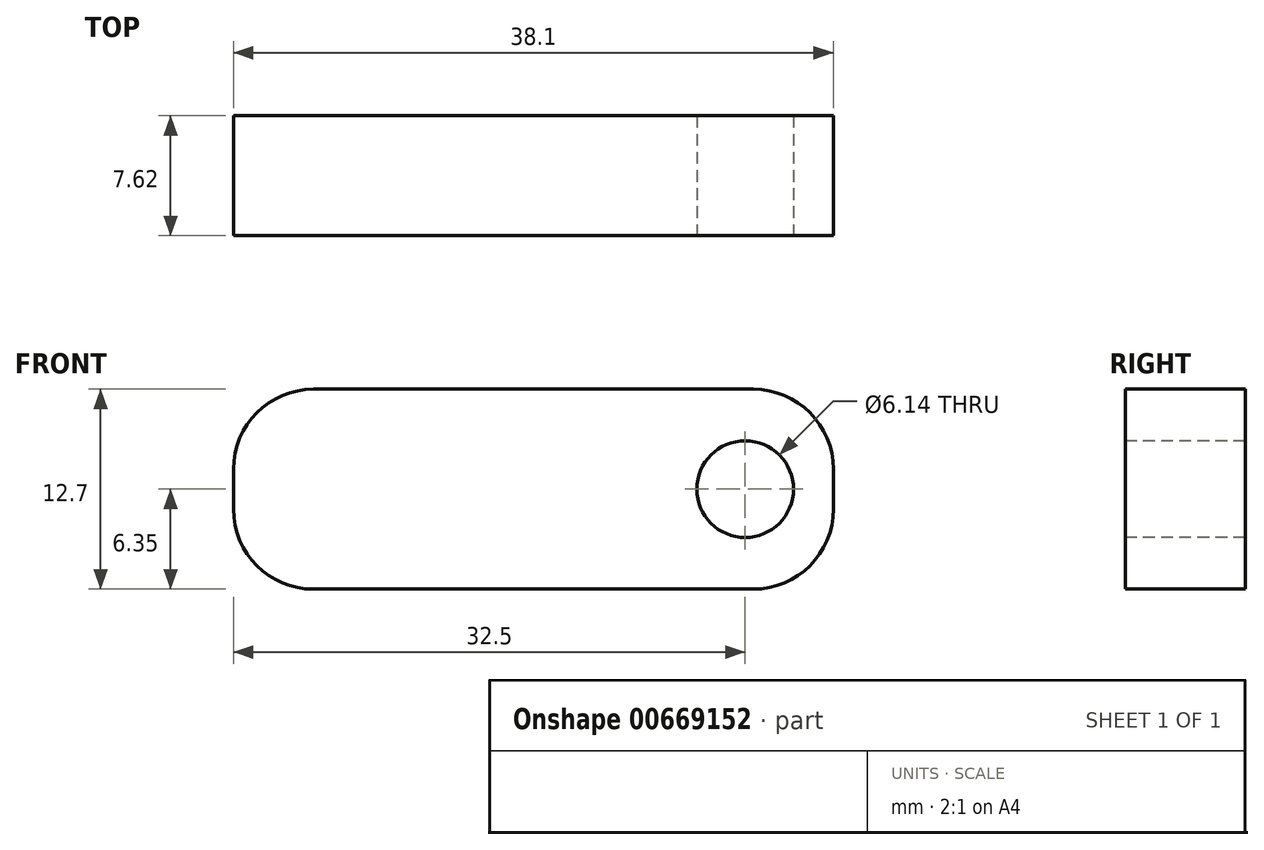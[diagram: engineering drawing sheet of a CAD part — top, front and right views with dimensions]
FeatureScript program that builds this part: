
annotation { "Feature Type Name" : "Feature", "Feature Type Description" : "" }
export const myFeature = defineFeature(function(context is Context, id is Id, definition is map)
    precondition{}
    {
        {
            var Q0;
            Q0=qCreatedBy(makeId("Front.planeOp"),FACE);
            var sketch = newSketch(context, id + "F0", { "sketchPlane" : qUnion([Q0])});
            skLineSegment(sketch, "E0.bottom", {"start": v(0, 0) * mm, "end": v(-38.1, 0) * mm});
            skLineSegment(sketch, "E0.top", {"start": v(0, 12.7) * mm, "end": v(-38.1, 12.7) * mm});
            skLineSegment(sketch, "E0.left", {"start": v(0, 0) * mm, "end": v(0, 12.7) * mm});
            skLineSegment(sketch, "E0.right", {"start": v(-38.1, 0) * mm, "end": v(-38.1, 12.7) * mm});
            skSolve(sketch);
        }
        {
            var Q0;
            Q0=makeQuery(id+"F0.imprint","IMPRINT",FACE,{"disambiguationData":[TD([[makeQuery(id+"F0.imprint","IMPRINT",EDGE,{"derivedFrom":sQuery(id+"F0.wireOp",EDGE,"E0.bottom")}),-1.0]])]});
            extrude(context, id + "F1", {"entities" : qUnion([Q0]), "depth" : 7.62 * mm, "offsetDistance" : 25.4 * mm});
        }
        {
            var Q0;
            Q0=makeQuery(id+"F1.opExtrude","CAP_FACE",FACE,{"disambiguationData":[OSD([sQuery(id+"F0.wireOp",EDGE,"E0.bottom"),sQuery(id+"F0.wireOp",EDGE,"E0.top"),sQuery(id+"F0.wireOp",EDGE,"E0.left"),sQuery(id+"F0.wireOp",EDGE,"E0.right")])],"isStart":false});
            var sketch = newSketch(context, id + "F2", { "sketchPlane" : qUnion([Q0])});
            skCircle(sketch, "E1", {"center": v(-5.6, 6.35) * mm, "radius": 3.07 * mm});
            skPoint(sketch, "E1.centerSnap0", {"position": v(0, 6.35) * mm});
            skSolve(sketch);
        }
        {
            var Q0;
            Q0=makeQuery(id+"F2.imprint","IMPRINT",FACE,{"disambiguationData":[TD([[makeQuery(id+"F2.imprint","IMPRINT",EDGE,{"derivedFrom":sQuery(id+"F2.wireOp",EDGE,"E1")}),1.0]])]});
            extrude(context, id + "F3", {"entities" : qUnion([Q0]), "operationType" : NewBodyOperationType.REMOVE, "endBound" : BoundingType.THROUGH_ALL, "oppositeDirection" : true, "depth" : 25.4 * mm, "offsetDistance" : 25.4 * mm});
        }
        {
            var Q0;
            Q0=makeQuery(id+"F1.opExtrude","SWEPT_EDGE",EDGE,{"disambiguationData":[OSD([sQuery(id+"F0.wireOp",EDGE,"E0.top"),sQuery(id+"F0.wireOp",EDGE,"E0.left")])]});
            var Q1;
            Q1=makeQuery(id+"F1.opExtrude","SWEPT_EDGE",EDGE,{"disambiguationData":[OSD([sQuery(id+"F0.wireOp",EDGE,"E0.bottom"),sQuery(id+"F0.wireOp",EDGE,"E0.left")])]});
            var Q2;
            Q2=makeQuery(id+"F1.opExtrude","SWEPT_EDGE",EDGE,{"disambiguationData":[OSD([sQuery(id+"F0.wireOp",EDGE,"E0.top"),sQuery(id+"F0.wireOp",EDGE,"E0.right")])]});
            var Q3;
            Q3=makeQuery(id+"F1.opExtrude","SWEPT_EDGE",EDGE,{"disambiguationData":[OSD([sQuery(id+"F0.wireOp",EDGE,"E0.bottom"),sQuery(id+"F0.wireOp",EDGE,"E0.right")])]});
            fillet(context, id + "F4", {"entities" : qUnion([Q0, Q1, Q2, Q3]), "radius" : 5.08 * mm, "tangentPropagation" : true, "allowEdgeOverflow" : false});
        }
    });
